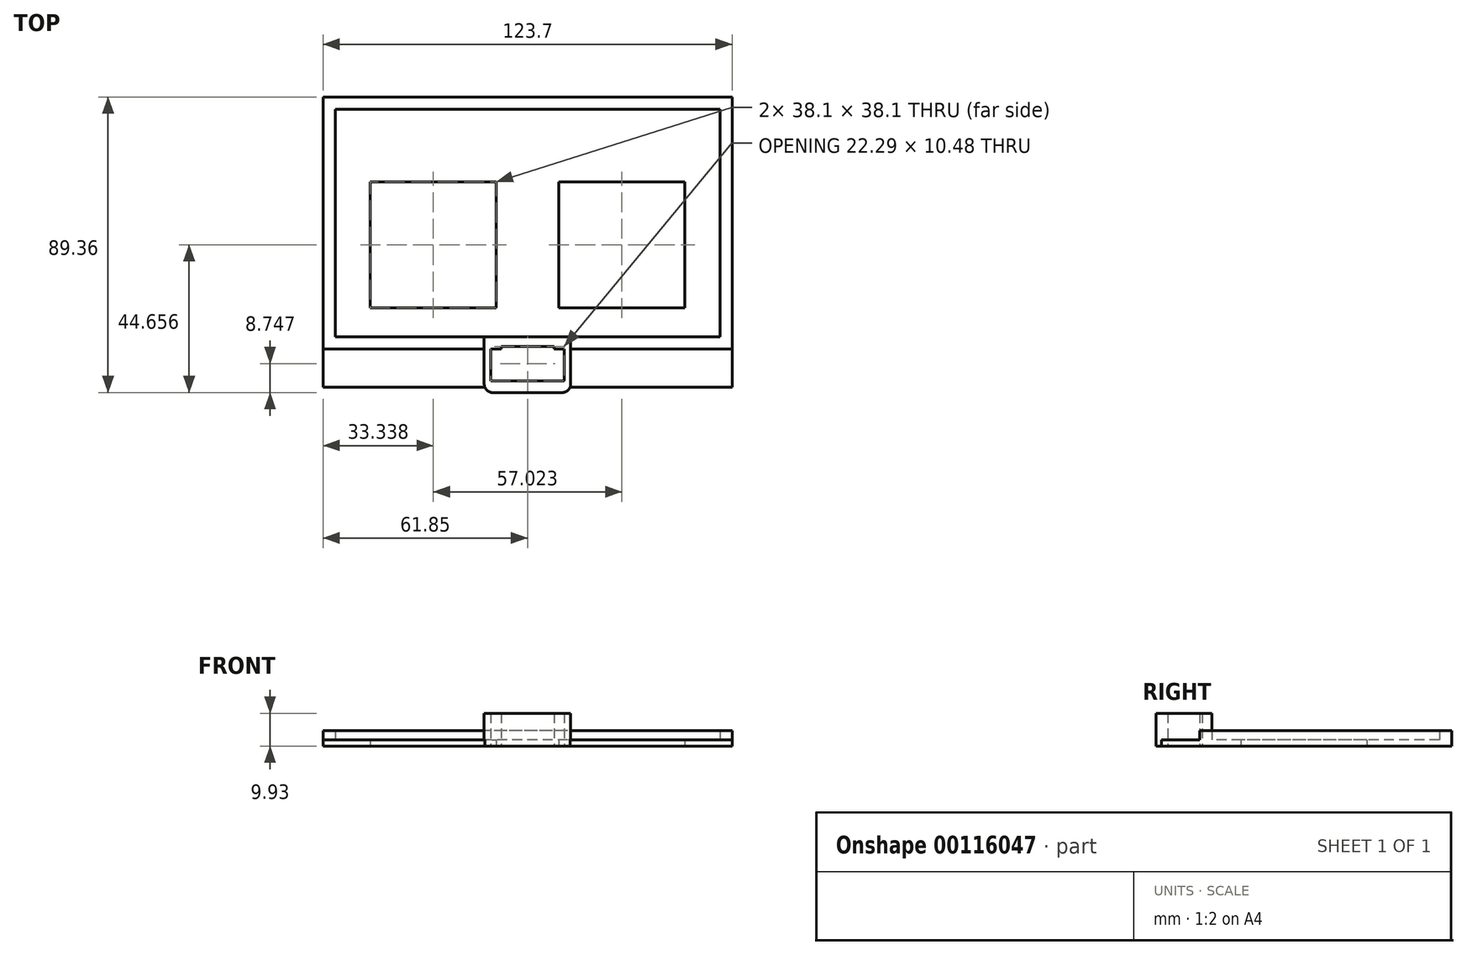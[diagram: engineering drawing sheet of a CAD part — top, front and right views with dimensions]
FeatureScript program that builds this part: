
annotation { "Feature Type Name" : "Feature", "Feature Type Description" : "" }
export const myFeature = defineFeature(function(context is Context, id is Id, definition is map)
    precondition{}
    {
        {
            var Q0;
            Q0=qCreatedBy(makeId("Top.planeOp"),FACE);
            var sketch = newSketch(context, id + "F0", { "sketchPlane" : qUnion([Q0])});
            skLineSegment(sketch, "E0.bottom", {"start": v(61.85, 38.1) * mm, "end": v(-61.85, 38.1) * mm});
            skLineSegment(sketch, "E0.top", {"start": v(61.85, -38.1) * mm, "end": v(-61.85, -38.1) * mm});
            skLineSegment(sketch, "E0.left", {"start": v(61.85, 38.1) * mm, "end": v(61.85, -49.66) * mm});
            skLineSegment(sketch, "E0.right", {"start": v(-61.85, 38.1) * mm, "end": v(-61.85, -49.66) * mm});
            skLineSegment(sketch, "E1.bottom", {"start": v(-11.14, -38.1) * mm, "end": v(11.14, -38.1) * mm});
            skLineSegment(sketch, "E1.top", {"start": v(-11.14, -47.75) * mm, "end": v(11.14, -47.75) * mm});
            skLineSegment(sketch, "E1.left", {"start": v(-11.14, -38.1) * mm, "end": v(-11.14, -47.75) * mm});
            skLineSegment(sketch, "E1.right", {"start": v(11.14, -38.1) * mm, "end": v(11.14, -47.75) * mm});
            skLineSegment(sketch, "E2.0", {"start": v(-13.1, -34.42) * mm, "end": v(-13.1, -51.26) * mm});
            skLineSegment(sketch, "E3.0", {"start": v(13.05, -34.42) * mm, "end": v(13.05, -51.26) * mm});
            skLineSegment(sketch, "E4.bottom", {"start": v(-8, -38.1) * mm, "end": v(8, -38.1) * mm});
            skLineSegment(sketch, "E4.top", {"start": v(-8, -37.27) * mm, "end": v(8, -37.27) * mm});
            skLineSegment(sketch, "E4.left", {"start": v(-8, -38.1) * mm, "end": v(-8, -37.27) * mm});
            skLineSegment(sketch, "E4.right", {"start": v(8, -38.1) * mm, "end": v(8, -37.27) * mm});
            skLineSegment(sketch, "E5.0", {"start": v(-13.1, -51.26) * mm, "end": v(13.05, -51.26) * mm});
            skLineSegment(sketch, "E6", {"start": v(6.8, -47.75) * mm, "end": v(6.8, -51.26) * mm});
            skLineSegment(sketch, "E7", {"start": v(-6.8, -47.75) * mm, "end": v(-6.8, -51.26) * mm});
            skLineSegment(sketch, "E8.0", {"start": v(58.17, 34.42) * mm, "end": v(-58.17, 34.42) * mm});
            skLineSegment(sketch, "E8.1", {"start": v(58.17, 34.42) * mm, "end": v(58.17, -34.42) * mm});
            skLineSegment(sketch, "E8.2", {"start": v(58.17, -34.42) * mm, "end": v(-58.17, -34.42) * mm});
            skLineSegment(sketch, "E8.3", {"start": v(-58.17, 34.42) * mm, "end": v(-58.17, -34.42) * mm});
            skLineSegment(sketch, "E9.bottom", {"start": v(-47.56, 12.45) * mm, "end": v(-9.46, 12.45) * mm});
            skLineSegment(sketch, "E9.top", {"start": v(-47.56, -25.65) * mm, "end": v(-9.46, -25.65) * mm});
            skLineSegment(sketch, "E9.left", {"start": v(-47.56, 12.45) * mm, "end": v(-47.56, -25.65) * mm});
            skLineSegment(sketch, "E9.right", {"start": v(-9.46, 12.45) * mm, "end": v(-9.46, -25.65) * mm});
            skLineSegment(sketch, "E10.MirrorCS", {"start": v(47.56, -25.65) * mm, "end": v(9.46, -25.65) * mm});
            skLineSegment(sketch, "E11.MirrorCS", {"start": v(9.46, 12.45) * mm, "end": v(9.46, -25.65) * mm});
            skLineSegment(sketch, "E12.MirrorCS", {"start": v(47.56, 12.45) * mm, "end": v(47.56, -25.65) * mm});
            skLineSegment(sketch, "E13.MirrorCS", {"start": v(47.56, 12.45) * mm, "end": v(9.46, 12.45) * mm});
            skLineSegment(sketch, "E14.0", {"start": v(61.85, -49.66) * mm, "end": v(13.05, -49.66) * mm});
            skLineSegment(sketch, "E15.trimOffspring", {"start": v(-13.1, -49.66) * mm, "end": v(-61.85, -49.66) * mm});
            skSolve(sketch);
        }
        {
            var Q0;
            Q0=makeQuery(id+"F0.imprint","IMPRINT",FACE,{"disambiguationData":[TD([[makeQuery(id+"F0.imprint","IMPRINT",EDGE,{"derivedFrom":sQuery(id+"F0.wireOp",EDGE,"URHqTRbd-ECci-eVHz-LjBZ-wQ03px0znPtk.bottom")}),-1.0]])]});
            var Q1;
            Q1=makeQuery(id+"F0.imprint","IMPRINT",FACE,{"disambiguationData":[TD([[makeQuery(id+"F0.imprint","IMPRINT",EDGE,{"derivedFrom":sQuery(id+"F0.wireOp",EDGE,"E8.0")}),1.0]])]});
            var Q2;
            {var subQ5=sQuery(id+"F0.wireOp",EDGE,"E15.trimOffspring");Q2=makeQuery(id+"F0.imprint","IMPRINT",FACE,{"disambiguationData":[TD([[makeQuery(id+"F0.imprint","IMPRINT",EDGE,{"derivedFrom":subQ5}),-1.0]])]});}
            var Q3;
            {var subQ5=sQuery(id+"F0.wireOp",EDGE,"E14.0");Q3=makeQuery(id+"F0.imprint","IMPRINT",FACE,{"disambiguationData":[TD([[makeQuery(id+"F0.imprint","IMPRINT",EDGE,{"derivedFrom":subQ5}),-1.0]])]});}
            extrude(context, id + "F1", {"entities" : qUnion([Q0, Q1, Q2, Q3]), "depth" : 1.9 * mm});
        }
        {
            var Q0;
            Q0=makeQuery(id+"F0.imprint","IMPRINT",FACE,{"disambiguationData":[TD([[makeQuery(id+"F0.imprint","IMPRINT",EDGE,{"derivedFrom":sQuery(id+"F0.wireOp",EDGE,"E0.bottom")}),1.0]])]});
            extrude(context, id + "F2", {"entities" : qUnion([Q0]), "operationType" : NewBodyOperationType.ADD, "depth" : 4.7 * mm});
        }
        {
            var Q0;
            Q0=makeQuery(id+"F0.imprint","IMPRINT",FACE,{"disambiguationData":[TD([[makeQuery(id+"F0.imprint","IMPRINT",EDGE,{"derivedFrom":sQuery(id+"F0.wireOp",EDGE,"E4.top")}),1.0]])]});
            var Q1;
            {var subQ5=sQuery(id+"F0.wireOp",EDGE,"E1.left");Q1=makeQuery(id+"F0.imprint","IMPRINT",FACE,{"disambiguationData":[TD([[makeQuery(id+"F0.imprint","IMPRINT",EDGE,{"derivedFrom":subQ5}),-1.0]])]});}
            var Q2;
            {var subQ6=sQuery(id+"F0.wireOp",EDGE,"E1.right");Q2=makeQuery(id+"F0.imprint","IMPRINT",FACE,{"disambiguationData":[TD([[makeQuery(id+"F0.imprint","IMPRINT",EDGE,{"derivedFrom":subQ6}),1.0]])]});}
            var Q3;
            {var subQ0=sQuery(id+"F0.wireOp",EDGE,"E6");Q3=makeQuery(id+"F0.imprint","IMPRINT",FACE,{"disambiguationData":[TD([[makeQuery(id+"F0.imprint","IMPRINT",EDGE,{"derivedFrom":subQ0}),-1.0]])]});}
            extrude(context, id + "F3", {"entities" : qUnion([Q0, Q1, Q2, Q3]), "operationType" : NewBodyOperationType.ADD, "depth" : 9.93 * mm});
        }
        {
            var Q0;
            Q0=makeQuery(id+"F3.opExtrude","SWEPT_EDGE",EDGE,{"disambiguationData":[OSD([sQuery(id+"F0.wireOp",EDGE,"E2.0"),sQuery(id+"F0.wireOp",EDGE,"E5.0")])]});
            var Q1;
            Q1=makeQuery(id+"F3.opExtrude","SWEPT_EDGE",EDGE,{"disambiguationData":[OSD([sQuery(id+"F0.wireOp",EDGE,"E3.0"),sQuery(id+"F0.wireOp",EDGE,"E5.0")])]});
            fillet(context, id + "F4", {"entities" : qUnion([Q0, Q1]), "radius" : 2.54 * mm, "tangentPropagation" : true, "allowEdgeOverflow" : false});
        }
    });
